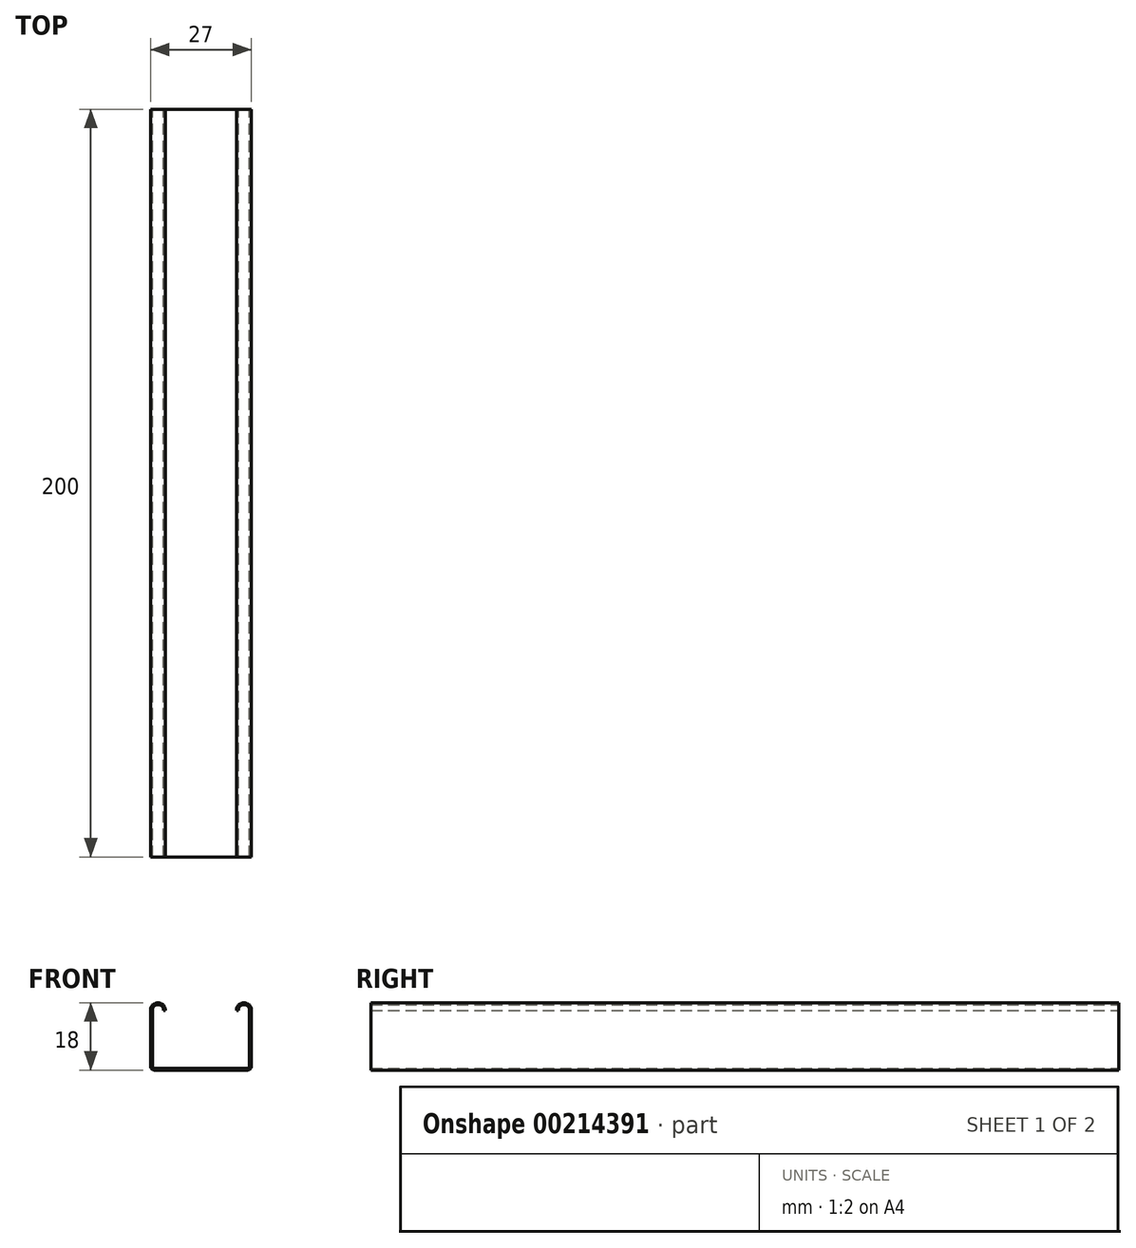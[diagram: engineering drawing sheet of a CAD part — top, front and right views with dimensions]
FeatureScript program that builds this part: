
annotation { "Feature Type Name" : "Feature", "Feature Type Description" : "" }
export const myFeature = defineFeature(function(context is Context, id is Id, definition is map)
    precondition{}
    {
        {
            var Q0;
            Q0=qCreatedBy(makeId("Front.planeOp"),FACE);
            var sketch = newSketch(context, id + "F0", { "sketchPlane" : qUnion([Q0])});
            skLineSegment(sketch, "E0.top", {"start": v(-13.5, -9) * mm, "end": v(13.5, -9) * mm});
            skLineSegment(sketch, "E0.left", {"start": v(-13.5, 7) * mm, "end": v(-13.5, -9) * mm});
            skLineSegment(sketch, "E0.right", {"start": v(13.5, 7) * mm, "end": v(13.5, -9) * mm});
            skArc(sketch, "E1", {"start": v(13.5, 7) * mm, "mid": v(11.5, 9) * mm, "end": v(9.5, 7) * mm});
            skArc(sketch, "E2", {"start": v(-9.5, 7) * mm, "mid": v(-11.5, 9) * mm, "end": v(-13.5, 7) * mm});
            skArc(sketch, "E3", {"start": v(13, 7) * mm, "mid": v(11.5, 8.5) * mm, "end": v(10, 7) * mm});
            skArc(sketch, "E4", {"start": v(-10, 7) * mm, "mid": v(-11.5, 8.5) * mm, "end": v(-13, 7) * mm});
            skLineSegment(sketch, "E5", {"start": v(-10, 7) * mm, "end": v(-9.5, 7) * mm});
            skLineSegment(sketch, "E6", {"start": v(10, 7) * mm, "end": v(9.5, 7) * mm});
            skLineSegment(sketch, "E7", {"start": v(-13, 7) * mm, "end": v(-13, -8.5) * mm});
            skLineSegment(sketch, "E8", {"start": v(-13, -8.5) * mm, "end": v(13, -8.5) * mm});
            skLineSegment(sketch, "E9", {"start": v(13, -8.5) * mm, "end": v(13, 7) * mm});
            skSolve(sketch);
        }
        {
            var Q0;
            Q0 = qSketchRegion(id + "F0", true);
            extrude(context, id + "F1", {"entities" : qUnion([Q0]), "depth" : 100 * mm, "hasSecondDirection" : true, "secondDirectionOppositeDirection" : true, "secondDirectionDepth" : 100 * mm});
        }
        {
            var Q0;
            Q0=makeQuery(id+"F1.opExtrude","SWEPT_EDGE",EDGE,{"disambiguationData":[OSD([sQuery(id+"F0.wireOp",EDGE,"E0.top"),sQuery(id+"F0.wireOp",EDGE,"E0.right")])]});
            var Q1;
            Q1=makeQuery(id+"F1.opExtrude","SWEPT_EDGE",EDGE,{"disambiguationData":[OSD([sQuery(id+"F0.wireOp",EDGE,"E0.top"),sQuery(id+"F0.wireOp",EDGE,"E0.left")])]});
            fillet(context, id + "F2", {"entities" : qUnion([Q0, Q1]), "radius" : 1 * mm, "tangentPropagation" : true, "allowEdgeOverflow" : false});
        }
        {
            var Q0;
            Q0=makeQuery(id+"F1.opExtrude","SWEPT_EDGE",EDGE,{"disambiguationData":[OSD([sQuery(id+"F0.wireOp",EDGE,"E7"),sQuery(id+"F0.wireOp",EDGE,"E8")])]});
            var Q1;
            Q1=makeQuery(id+"F1.opExtrude","SWEPT_EDGE",EDGE,{"disambiguationData":[OSD([sQuery(id+"F0.wireOp",EDGE,"E8"),sQuery(id+"F0.wireOp",EDGE,"E9")])]});
            fillet(context, id + "F3", {"entities" : qUnion([Q0, Q1]), "radius" : .5 * mm, "tangentPropagation" : true, "allowEdgeOverflow" : false});
        }
    });
